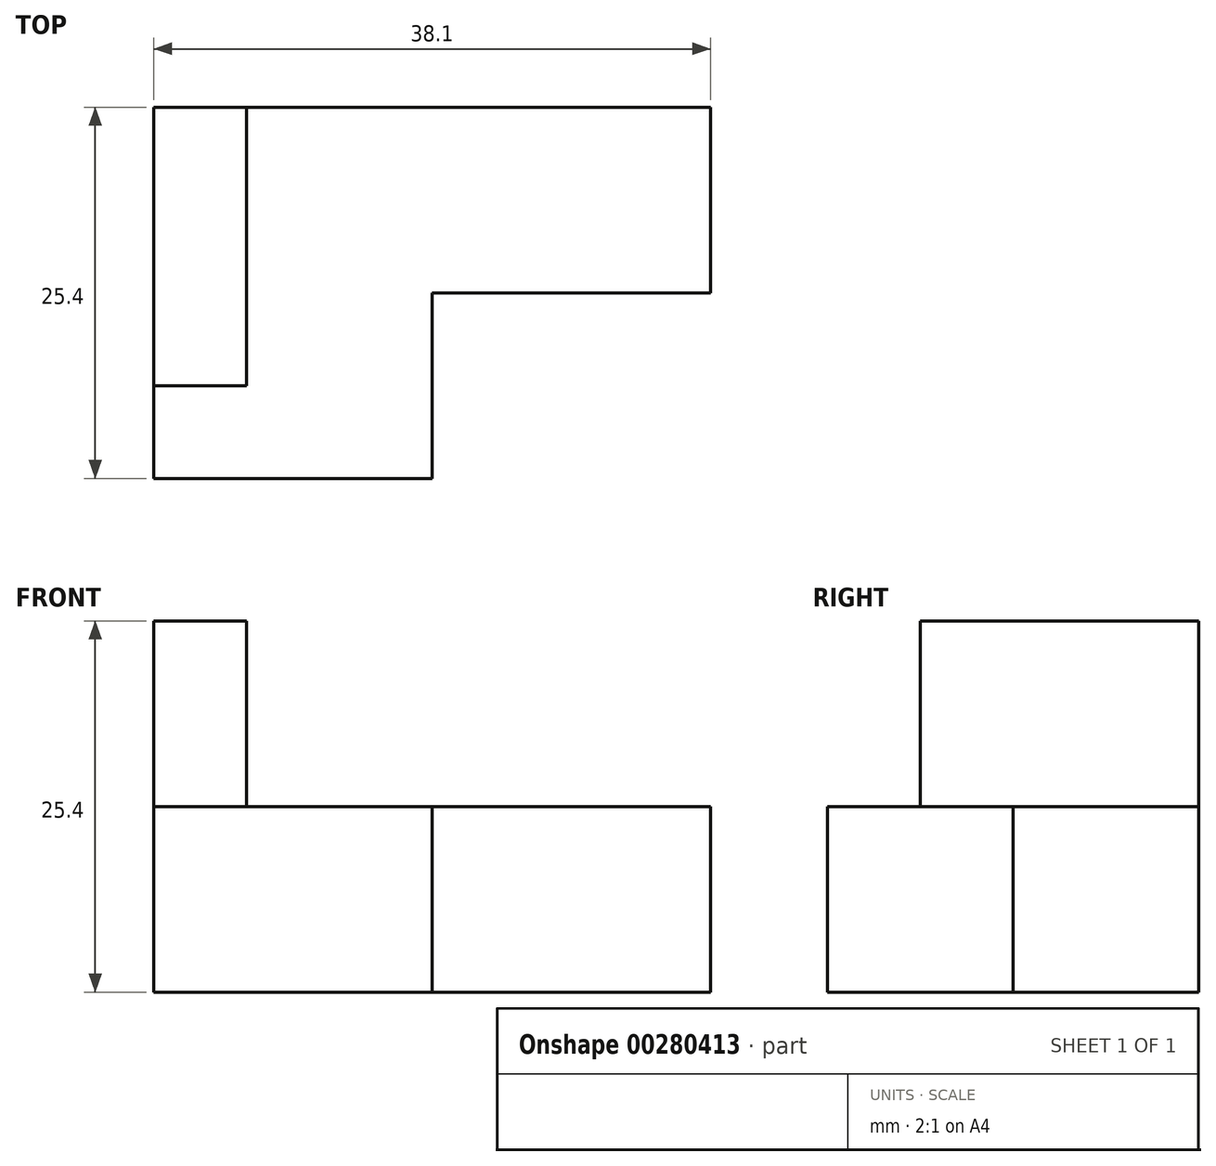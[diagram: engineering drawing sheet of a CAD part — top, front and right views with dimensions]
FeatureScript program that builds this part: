
annotation { "Feature Type Name" : "Feature", "Feature Type Description" : "" }
export const myFeature = defineFeature(function(context is Context, id is Id, definition is map)
    precondition{}
    {
        {
            var Q0;
            Q0=qCreatedBy(makeId("Front.planeOp"),FACE);
            var sketch = newSketch(context, id + "F0", { "sketchPlane" : qUnion([Q0])});
            skLineSegment(sketch, "E0", {"start": v(0, 0) * mm, "end": v(0, 12.7) * mm});
            skLineSegment(sketch, "E1", {"start": v(0, 12.7) * mm, "end": v(38.1, 12.7) * mm});
            skLineSegment(sketch, "E2", {"start": v(38.1, 12.7) * mm, "end": v(38.1, 0) * mm});
            skLineSegment(sketch, "E3", {"start": v(38.1, 0) * mm, "end": v(0, 0) * mm});
            skSolve(sketch);
        }
        {
            var Q0;
            Q0=makeQuery(id+"F0.imprint","IMPRINT",FACE,{"disambiguationData":[TD([[makeQuery(id+"F0.imprint","IMPRINT",EDGE,{"derivedFrom":sQuery(id+"F0.wireOp",EDGE,"E0")}),-1.0]])]});
            extrude(context, id + "F1", {"entities" : qUnion([Q0]), "depth" : 25.4 * mm});
        }
        {
            var Q0;
            Q0=qCreatedBy(makeId("Top.planeOp"),FACE);
            var sketch = newSketch(context, id + "F2", { "sketchPlane" : qUnion([Q0])});
            skLineSegment(sketch, "E4.bottom", {"start": v(38.1, -25.4) * mm, "end": v(19.05, -25.4) * mm});
            skLineSegment(sketch, "E4.top", {"start": v(38.1, -12.7) * mm, "end": v(19.05, -12.7) * mm});
            skLineSegment(sketch, "E4.left", {"start": v(38.1, -25.4) * mm, "end": v(38.1, -12.7) * mm});
            skLineSegment(sketch, "E4.right", {"start": v(19.05, -25.4) * mm, "end": v(19.05, -12.7) * mm});
            skSolve(sketch);
        }
        {
            var Q0;
            Q0 = qSketchRegion(id + "F2", true);
            extrude(context, id + "F3", {"entities" : qUnion([Q0]), "operationType" : NewBodyOperationType.REMOVE, "depth" : 25.4 * mm});
        }
        {
            var Q0;
            Q0=makeQuery(id+"F1.opExtrude","SWEPT_FACE",FACE,{"disambiguationData":[OSD([sQuery(id+"F0.wireOp",EDGE,"E1")])]});
            var sketch = newSketch(context, id + "F4", { "sketchPlane" : qUnion([Q0])});
            skLineSegment(sketch, "E5.bottom", {"start": v(0, 0) * mm, "end": v(6.35, 0) * mm});
            skLineSegment(sketch, "E5.top", {"start": v(0, -19.05) * mm, "end": v(6.35, -19.05) * mm});
            skLineSegment(sketch, "E5.left", {"start": v(0, 0) * mm, "end": v(0, -19.05) * mm});
            skLineSegment(sketch, "E5.right", {"start": v(6.35, 0) * mm, "end": v(6.35, -19.05) * mm});
            skSolve(sketch);
        }
        {
            var Q0;
            Q0 = qSketchRegion(id + "F4", true);
            extrude(context, id + "F5", {"entities" : qUnion([Q0]), "operationType" : NewBodyOperationType.ADD, "depth" : 12.7 * mm});
        }
    });
